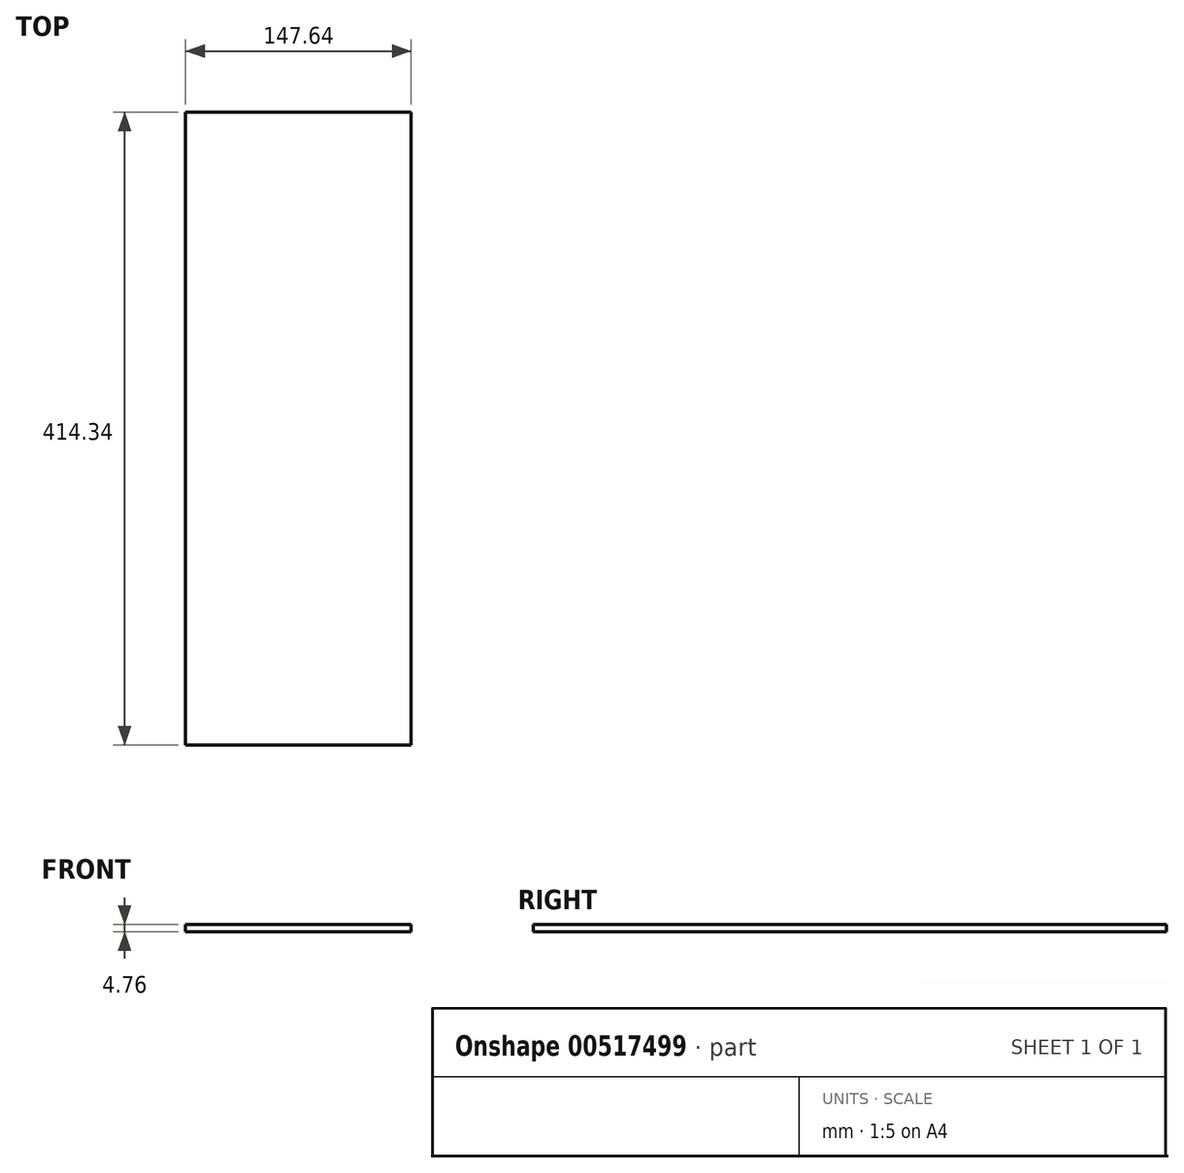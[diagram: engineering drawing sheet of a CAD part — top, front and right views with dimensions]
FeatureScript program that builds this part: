
annotation { "Feature Type Name" : "Feature", "Feature Type Description" : "" }
export const myFeature = defineFeature(function(context is Context, id is Id, definition is map)
    precondition{}
    {
        {
            var Q0;
            Q0=qCreatedBy(makeId("Top.planeOp"),FACE);
            var sketch = newSketch(context, id + "F0", { "sketchPlane" : qUnion([Q0])});
            skLineSegment(sketch, "E0.bottom", {"start": v(-73.82, 207.17) * mm, "end": v(73.82, 207.17) * mm});
            skLineSegment(sketch, "E0.top", {"start": v(-73.82, -207.17) * mm, "end": v(73.82, -207.17) * mm});
            skLineSegment(sketch, "E0.left", {"start": v(-73.82, 207.17) * mm, "end": v(-73.82, -207.17) * mm});
            skLineSegment(sketch, "E0.right", {"start": v(73.82, 207.17) * mm, "end": v(73.82, -207.17) * mm});
            skPoint(sketch, "E0.middle", {"position": v(0, 0) * mm});
            skSolve(sketch);
        }
        {
            var Q0;
            Q0 = qSketchRegion(id + "F0", true);
            extrude(context, id + "F1", {"entities" : qUnion([Q0]), "depth" : 4.76 * mm, "offsetDistance" : 25.4 * mm});
        }
    });
